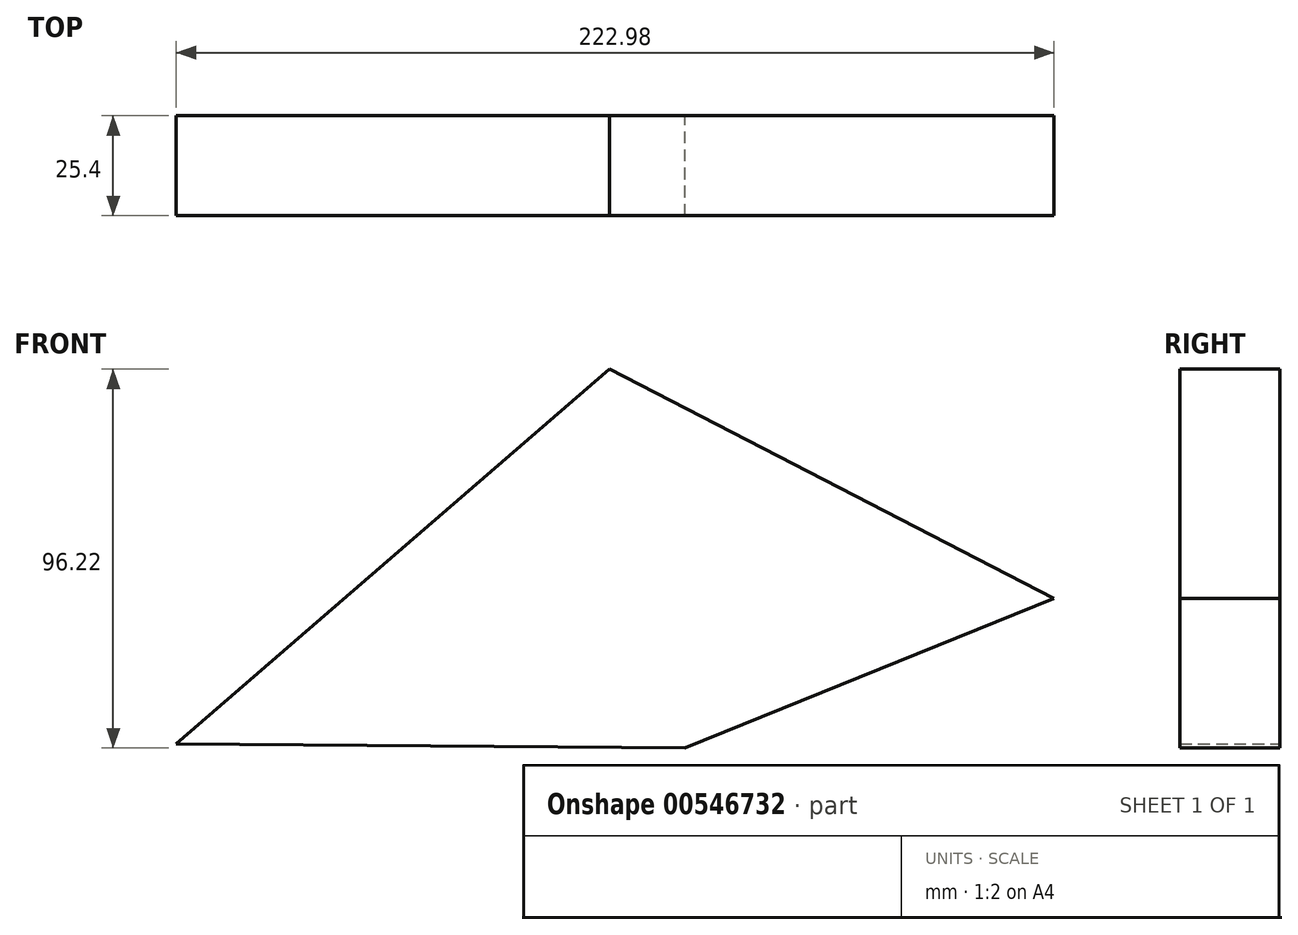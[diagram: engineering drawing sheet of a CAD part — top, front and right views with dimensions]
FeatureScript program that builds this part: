
annotation { "Feature Type Name" : "Feature", "Feature Type Description" : "" }
export const myFeature = defineFeature(function(context is Context, id is Id, definition is map)
    precondition{}
    {
        {
            var Q0;
            Q0=qCreatedBy(makeId("Front.planeOp"),FACE);
            var sketch = newSketch(context, id + "F0", { "sketchPlane" : qUnion([Q0])});
            skLineSegment(sketch, "E0", {"start": v(-115.77, -14.76) * mm, "end": v(-5.65, 80.42) * mm});
            skLineSegment(sketch, "E1", {"start": v(-5.65, 80.42) * mm, "end": v(107.2, 22.18) * mm});
            skLineSegment(sketch, "E2", {"start": v(107.2, 22.18) * mm, "end": v(13.41, -15.8) * mm});
            skLineSegment(sketch, "E3", {"start": v(13.41, -15.8) * mm, "end": v(-115.77, -14.76) * mm});
            skSolve(sketch);
        }
        {
            var Q0;
            Q0=makeQuery(id+"F0.imprint","IMPRINT",FACE,{"disambiguationData":[TD([[makeQuery(id+"F0.imprint","IMPRINT",EDGE,{"derivedFrom":sQuery(id+"F0.wireOp",EDGE,"E0")}),-1.0]])]});
            extrude(context, id + "F1", {"entities" : qUnion([Q0]), "depth" : 25.4 * mm, "offsetDistance" : 25.4 * mm});
        }
    });
